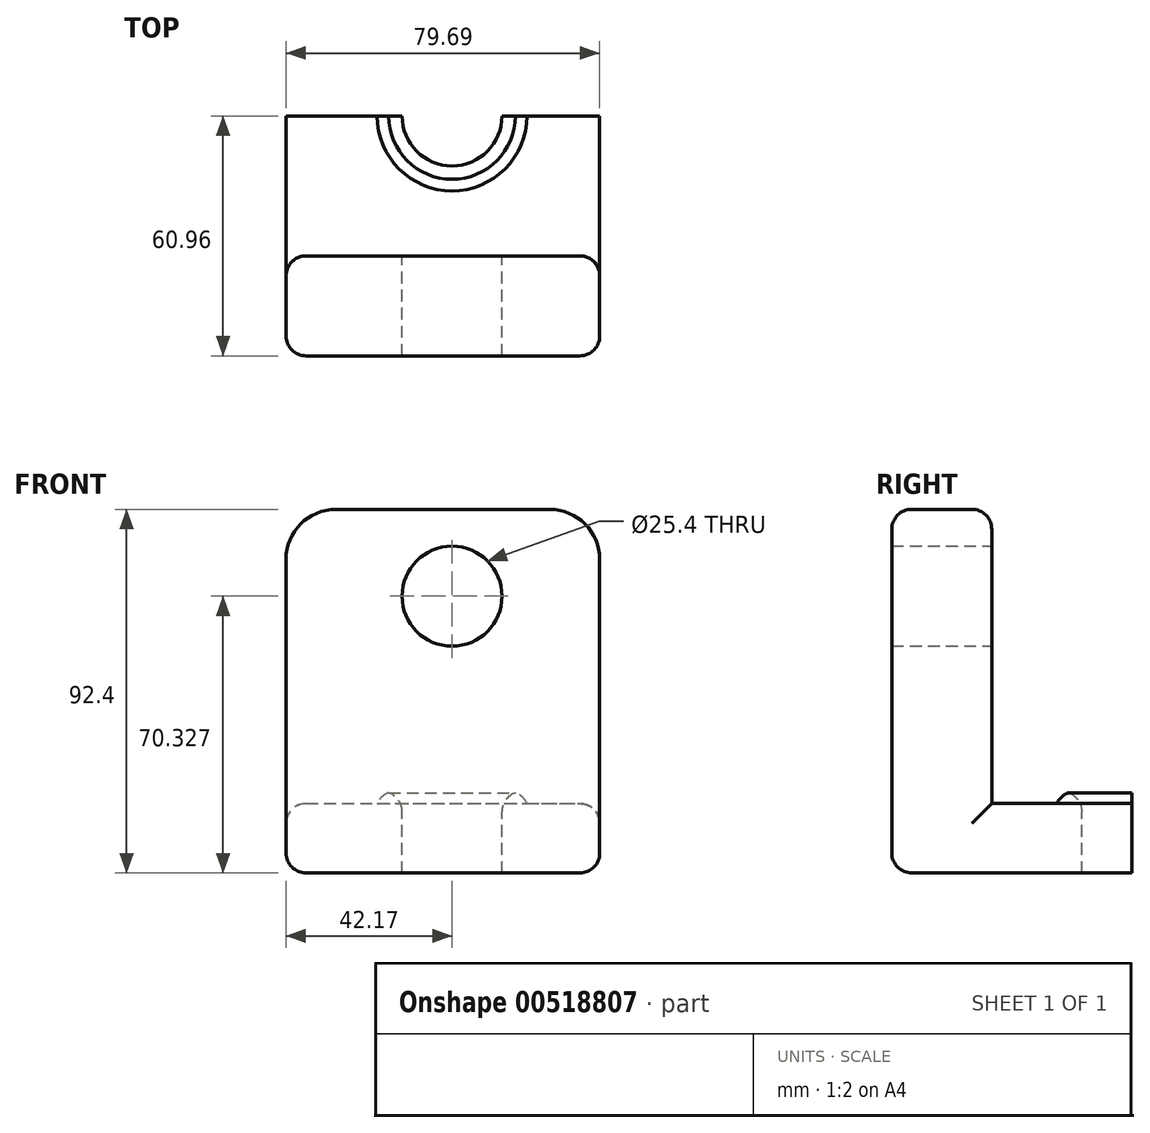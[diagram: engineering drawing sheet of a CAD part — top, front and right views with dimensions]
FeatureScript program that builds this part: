
annotation { "Feature Type Name" : "Feature", "Feature Type Description" : "" }
export const myFeature = defineFeature(function(context is Context, id is Id, definition is map)
    precondition{}
    {
        {
            var Q0;
            Q0=qCreatedBy(makeId("Front.planeOp"),FACE);
            var sketch = newSketch(context, id + "F0", { "sketchPlane" : qUnion([Q0])});
            skLineSegment(sketch, "E0.bottom", {"start": v(-42.17, 53.46) * mm, "end": v(37.52, 53.46) * mm});
            skLineSegment(sketch, "E0.top", {"start": v(-42.17, -38.94) * mm, "end": v(37.52, -38.94) * mm});
            skLineSegment(sketch, "E0.left", {"start": v(-42.17, 53.46) * mm, "end": v(-42.17, -38.94) * mm});
            skLineSegment(sketch, "E0.right", {"start": v(37.52, 53.46) * mm, "end": v(37.52, -38.94) * mm});
            skLineSegment(sketch, "E1", {"start": v(-42.17, -21.3) * mm, "end": v(37.52, -21.3) * mm});
            skCircle(sketch, "E2", {"center": v(0, 31.39) * mm, "radius": 12.7 * mm});
            skSolve(sketch);
        }
        {
            var Q0;
            Q0 = qSketchRegion(id + "F0", true);
            extrude(context, id + "F1", {"entities" : qUnion([Q0]), "depth" : 25.4 * mm, "offsetDistance" : 25.4 * mm});
        }
        {
            var Q0;
            {var subQ0=sQuery(id+"F0.wireOp",EDGE,"E0.top");Q0=makeQuery(id+"F0.imprint","IMPRINT",FACE,{"disambiguationData":[TD([[makeQuery(id+"F0.imprint","IMPRINT",EDGE,{"derivedFrom":subQ0}),1.0]])]});}
            extrude(context, id + "F2", {"entities" : qUnion([Q0]), "operationType" : NewBodyOperationType.ADD, "oppositeDirection" : true, "depth" : 35.56 * mm, "offsetDistance" : 25.4 * mm});
        }
        {
            var Q0;
            Q0=makeQuery(id+"F2.opExtrude","SWEPT_FACE",FACE,{"disambiguationData":[OSD([sQuery(id+"F0.wireOp",EDGE,"E1")])]});
            var sketch = newSketch(context, id + "F3", { "sketchPlane" : qUnion([Q0])});
            skCircle(sketch, "E3", {"center": v(0, 35.56) * mm, "radius": 12.7 * mm});
            skCircle(sketch, "E4", {"center": v(0, 35.56) * mm, "radius": 19.05 * mm});
            skSolve(sketch);
        }
        {
            var Q0;
            {var subQ0=sQuery(id+"F3.wireOp",EDGE,"E3");var subQ1=makeQuery(id+"F2.opExtrude","CAP_EDGE",EDGE,{"disambiguationData":[OSD([sQuery(id+"F0.wireOp",EDGE,"E1")])],"isStart":false});var subQ2=makeQuery(id+"F3.imprint","INTERSECT",VERTEX,{"disambiguationData":[OD(0.0)],"derivedFrom":[subQ1,subQ0]});Q0=makeQuery(id+"F3.imprint","IMPRINT",FACE,{"disambiguationData":[TD([[makeQuery(id+"F3.imprint","IMPRINT",EDGE,{"disambiguationData":[TD([[subQ2,-1.0]])],"derivedFrom":subQ0}),1.0]])]});}
            var Q1;
            Q1=sQuery(id+"F3.wireOp",EDGE,"E3");
            extrude(context, id + "F4", {"entities" : qUnion([Q0]), "operationType" : NewBodyOperationType.REMOVE, "surfaceEntities" : qUnion([Q1]), "endBound" : BoundingType.THROUGH_ALL, "oppositeDirection" : true, "depth" : 25.4 * mm, "offsetDistance" : 25.4 * mm});
        }
        {
            var Q0;
            Q0=makeQuery(id+"F1.opExtrude","SWEPT_EDGE",EDGE,{"disambiguationData":[OSD([sQuery(id+"F0.wireOp",EDGE,"E0.bottom"),sQuery(id+"F0.wireOp",EDGE,"E0.left")])]});
            var Q1;
            Q1=makeQuery(id+"F1.opExtrude","SWEPT_EDGE",EDGE,{"disambiguationData":[OSD([sQuery(id+"F0.wireOp",EDGE,"E0.bottom"),sQuery(id+"F0.wireOp",EDGE,"E0.right")])]});
            fillet(context, id + "F5", {"entities" : qUnion([Q0, Q1]), "radius" : 12.7 * mm, "tangentPropagation" : true, "allowEdgeOverflow" : false});
        }
        {
            var Q0;
            Q0=makeQuery(id+"F1.opExtrude","CAP_EDGE",EDGE,{"disambiguationData":[OSD([sQuery(id+"F0.wireOp",EDGE,"E0.bottom")])],"isStart":true});
            var Q1;
            Q1=makeQuery(id+"F1.opExtrude","CAP_EDGE",EDGE,{"disambiguationData":[OSD([sQuery(id+"F0.wireOp",EDGE,"E0.bottom")])],"isStart":false});
            var Q2;
            Q2=makeQuery(id+"F1.opExtrude","CAP_EDGE",EDGE,{"disambiguationData":[OSD([sQuery(id+"F0.wireOp",EDGE,"E0.left")])],"isStart":true});
            var Q3;
            Q3=makeQuery(id+"F1.opExtrude","CAP_EDGE",EDGE,{"disambiguationData":[OSD([sQuery(id+"F0.wireOp",EDGE,"E0.right")])],"isStart":true});
            var Q4;
            Q4=makeQuery(id+"F2.opExtrude","CAP_EDGE",EDGE,{"disambiguationData":[OSD([sQuery(id+"F0.wireOp",EDGE,"E1")])],"isStart":true});
            var Q5;
            Q5=makeQuery(id+"F2.opExtrude","SWEPT_EDGE",EDGE,{"disambiguationData":[OSD([sQuery(id+"F0.wireOp",EDGE,"E0.right"),sQuery(id+"F0.wireOp",EDGE,"E1")])]});
            var Q6;
            Q6=makeQuery(id+"F2.opExtrude","SWEPT_EDGE",EDGE,{"disambiguationData":[OSD([sQuery(id+"F0.wireOp",EDGE,"E0.left"),sQuery(id+"F0.wireOp",EDGE,"E1")])]});
            var Q7;
            Q7=makeQuery(id+"F1.opExtrude","CAP_EDGE",EDGE,{"disambiguationData":[OSD([sQuery(id+"F0.wireOp",EDGE,"E0.left")])],"isStart":false});
            var Q8;
            {var subQ0=sQuery(id+"F0.wireOp",EDGE,"E0.left");var subQ1=sQuery(id+"F0.wireOp",EDGE,"E0.top");Q8=makeQuery(id+"F2.boolean.opBoolean","MERGE",EDGE,{"derivedFrom":[makeQuery(id+"F1.opExtrude","SWEPT_EDGE",EDGE,{"disambiguationData":[OSD([subQ1,subQ0])]}),makeQuery(id+"F2.opExtrude","SWEPT_EDGE",EDGE,{"disambiguationData":[OSD([subQ1,subQ0])]})]});}
            var Q9;
            Q9=makeQuery(id+"F1.opExtrude","CAP_EDGE",EDGE,{"disambiguationData":[OSD([sQuery(id+"F0.wireOp",EDGE,"E0.right")])],"isStart":false});
            var Q10;
            {var subQ0=sQuery(id+"F0.wireOp",EDGE,"E0.right");var subQ1=sQuery(id+"F0.wireOp",EDGE,"E0.top");Q10=makeQuery(id+"F2.boolean.opBoolean","MERGE",EDGE,{"derivedFrom":[makeQuery(id+"F1.opExtrude","SWEPT_EDGE",EDGE,{"disambiguationData":[OSD([subQ1,subQ0])]}),makeQuery(id+"F2.opExtrude","SWEPT_EDGE",EDGE,{"disambiguationData":[OSD([subQ1,subQ0])]})]});}
            fillet(context, id + "F6", {"entities" : qUnion([Q0, Q1, Q2, Q3, Q4, Q5, Q6, Q7, Q8, Q9, Q10]), "radius" : 5.08 * mm, "tangentPropagation" : true, "allowEdgeOverflow" : false});
        }
        {
            var Q0;
            Q0=makeQuery(id+"F1.opExtrude","CAP_EDGE",EDGE,{"disambiguationData":[OSD([sQuery(id+"F0.wireOp",EDGE,"E0.top")])],"isStart":false});
            fillet(context, id + "F7", {"entities" : qUnion([Q0]), "radius" : 5.08 * mm, "tangentPropagation" : true, "allowEdgeOverflow" : false});
        }
        {
            var Q0;
            {var subQ0=sQuery(id+"F3.wireOp",EDGE,"E3");var subQ1=makeQuery(id+"F2.opExtrude","CAP_EDGE",EDGE,{"disambiguationData":[OSD([sQuery(id+"F0.wireOp",EDGE,"E1")])],"isStart":false});var subQ2=makeQuery(id+"F3.imprint","INTERSECT",VERTEX,{"disambiguationData":[OD(0.0)],"derivedFrom":[subQ1,subQ0]});Q0=makeQuery(id+"F3.imprint","IMPRINT",FACE,{"disambiguationData":[TD([[makeQuery(id+"F3.imprint","IMPRINT",EDGE,{"disambiguationData":[TD([[subQ2,-1.0]])],"derivedFrom":subQ0}),-1.0]])]});}
            extrude(context, id + "F8", {"entities" : qUnion([Q0]), "operationType" : NewBodyOperationType.ADD, "depth" : 3.05 * mm, "offsetDistance" : 25.4 * mm});
        }
        {
            var Q0;
            Q0=makeQuery(id+"F8.opExtrude","CAP_EDGE",EDGE,{"disambiguationData":[OSD([sQuery(id+"F3.wireOp",EDGE,"E4")])],"isStart":false});
            var Q1;
            Q1=makeQuery(id+"F8.opExtrude","CAP_EDGE",EDGE,{"disambiguationData":[OSD([sQuery(id+"F3.wireOp",EDGE,"E3")])],"isStart":false});
            fillet(context, id + "F9", {"entities" : qUnion([Q0, Q1]), "radius" : 5.08 * mm, "tangentPropagation" : true, "allowEdgeOverflow" : false});
        }
    });
